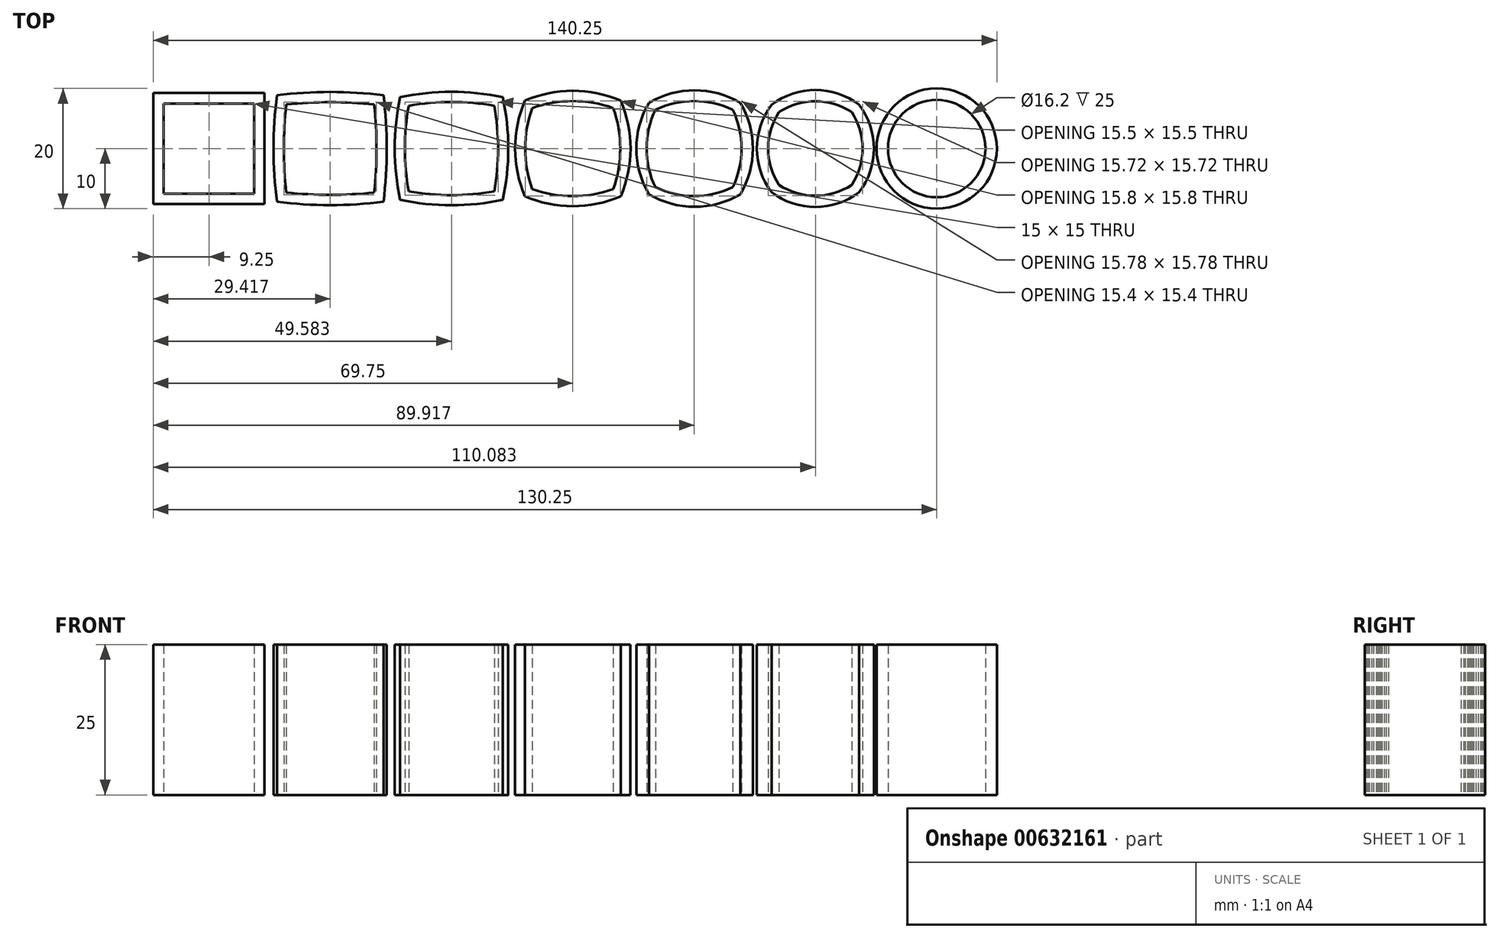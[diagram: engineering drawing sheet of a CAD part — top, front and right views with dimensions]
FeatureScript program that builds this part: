
annotation { "Feature Type Name" : "Feature", "Feature Type Description" : "" }
export const myFeature = defineFeature(function(context is Context, id is Id, definition is map)
    precondition{}
    {
        {
            var Q0;
            Q0=qCreatedBy(makeId("Top.planeOp"),FACE);
            var sketch = newSketch(context, id + "F0", { "sketchPlane" : qUnion([Q0])});
            skLineSegment(sketch, "E0", {"start": v(-60.5, 0) * mm, "end": v(-40.33, 0) * mm, "construction": true});
            skLineSegment(sketch, "E1", {"start": v(-40.33, 0) * mm, "end": v(-20.17, 0) * mm, "construction": true});
            skLineSegment(sketch, "E2", {"start": v(-20.17, 0) * mm, "end": v(0, 0) * mm, "construction": true});
            skLineSegment(sketch, "E3", {"start": v(0, 0) * mm, "end": v(20.17, 0) * mm, "construction": true});
            skLineSegment(sketch, "E4", {"start": v(20.17, 0) * mm, "end": v(40.33, 0) * mm, "construction": true});
            skLineSegment(sketch, "E5", {"start": v(40.33, 0) * mm, "end": v(60.5, 0) * mm, "construction": true});
            skCircle(sketch, "E6", {"center": v(60.5, 0) * mm, "radius": 8.1 * mm});
            skCircle(sketch, "E7", {"center": v(60.5, 0) * mm, "radius": 10 * mm});
            skLineSegment(sketch, "E8.bottom", {"start": v(-68, 7.5) * mm, "end": v(-53, 7.5) * mm});
            skLineSegment(sketch, "E8.top", {"start": v(-68, -7.5) * mm, "end": v(-53, -7.5) * mm});
            skLineSegment(sketch, "E8.left", {"start": v(-68, 7.5) * mm, "end": v(-68, -7.5) * mm});
            skLineSegment(sketch, "E8.right", {"start": v(-53, 7.5) * mm, "end": v(-53, -7.5) * mm});
            skPoint(sketch, "E8.middle", {"position": v(-60.5, 0) * mm});
            skLineSegment(sketch, "E9.bottom", {"start": v(-69.75, 9.25) * mm, "end": v(-51.25, 9.25) * mm});
            skLineSegment(sketch, "E9.top", {"start": v(-69.75, -9.25) * mm, "end": v(-51.25, -9.25) * mm});
            skLineSegment(sketch, "E9.left", {"start": v(-69.75, 9.25) * mm, "end": v(-69.75, -9.25) * mm});
            skLineSegment(sketch, "E9.right", {"start": v(-51.25, 9.25) * mm, "end": v(-51.25, -9.25) * mm});
            skArc(sketch, "E10", {"start": v(-33.02, -7.32) * mm, "mid": v(-32.63, 0) * mm, "end": v(-33.02, 7.32) * mm});
            skArc(sketch, "E11", {"start": v(-33.02, 7.32) * mm, "mid": v(-40.33, 7.7) * mm, "end": v(-47.65, 7.32) * mm});
            skArc(sketch, "E12", {"start": v(-47.65, 7.32) * mm, "mid": v(-48.03, 0) * mm, "end": v(-47.65, -7.32) * mm});
            skArc(sketch, "E13", {"start": v(-47.65, -7.32) * mm, "mid": v(-40.33, -7.7) * mm, "end": v(-33.02, -7.32) * mm});
            skArc(sketch, "E14", {"start": v(-31.48, -8.85) * mm, "mid": v(-30.92, 0) * mm, "end": v(-31.48, 8.85) * mm});
            skArc(sketch, "E15", {"start": v(-31.48, 8.85) * mm, "mid": v(-40.33, 9.41) * mm, "end": v(-49.18, 8.85) * mm});
            skArc(sketch, "E16", {"start": v(-49.18, 8.85) * mm, "mid": v(-49.75, 0) * mm, "end": v(-49.18, -8.85) * mm});
            skArc(sketch, "E17", {"start": v(-49.18, -8.85) * mm, "mid": v(-40.33, -9.41) * mm, "end": v(-31.48, -8.85) * mm});
            skArc(sketch, "E18", {"start": v(-13.05, -7.11) * mm, "mid": v(-12.42, 0) * mm, "end": v(-13.05, 7.11) * mm});
            skArc(sketch, "E19", {"start": v(-13.05, 7.11) * mm, "mid": v(-20.17, 7.75) * mm, "end": v(-27.28, 7.11) * mm});
            skArc(sketch, "E20", {"start": v(-27.28, 7.11) * mm, "mid": v(-27.92, 0) * mm, "end": v(-27.28, -7.11) * mm});
            skArc(sketch, "E21", {"start": v(-27.28, -7.11) * mm, "mid": v(-20.17, -7.75) * mm, "end": v(-13.05, -7.11) * mm});
            skArc(sketch, "E22", {"start": v(-11.64, -8.53) * mm, "mid": v(-10.72, 0) * mm, "end": v(-11.64, 8.53) * mm});
            skArc(sketch, "E23", {"start": v(-11.64, 8.53) * mm, "mid": v(-20.17, 9.45) * mm, "end": v(-28.7, 8.53) * mm});
            skArc(sketch, "E24", {"start": v(-28.7, 8.53) * mm, "mid": v(-29.61, 0) * mm, "end": v(-28.7, -8.53) * mm});
            skArc(sketch, "E25", {"start": v(-28.7, -8.53) * mm, "mid": v(-20.17, -9.45) * mm, "end": v(-11.64, -8.53) * mm});
            skArc(sketch, "E26", {"start": v(6.73, -6.73) * mm, "mid": v(7.9, 0) * mm, "end": v(6.73, 6.73) * mm});
            skArc(sketch, "E27", {"start": v(6.73, 6.73) * mm, "mid": v(0, 7.9) * mm, "end": v(-6.73, 6.73) * mm});
            skArc(sketch, "E28", {"start": v(-6.73, 6.73) * mm, "mid": v(-7.9, 0) * mm, "end": v(-6.73, -6.73) * mm});
            skArc(sketch, "E29", {"start": v(-6.73, -6.73) * mm, "mid": v(0, -7.9) * mm, "end": v(6.73, -6.73) * mm});
            skArc(sketch, "E30", {"start": v(7.95, -7.95) * mm, "mid": v(9.6, 0) * mm, "end": v(7.95, 7.95) * mm});
            skArc(sketch, "E31", {"start": v(7.95, 7.95) * mm, "mid": v(0, 9.6) * mm, "end": v(-7.95, 7.95) * mm});
            skArc(sketch, "E32", {"start": v(-7.95, 7.95) * mm, "mid": v(-9.6, 0) * mm, "end": v(-7.95, -7.95) * mm});
            skArc(sketch, "E33", {"start": v(-7.95, -7.95) * mm, "mid": v(0, -9.6) * mm, "end": v(7.95, -7.95) * mm});
            skArc(sketch, "E34", {"start": v(26.6, -6.44) * mm, "mid": v(28.06, 0) * mm, "end": v(26.6, 6.44) * mm});
            skArc(sketch, "E35", {"start": v(26.6, 6.44) * mm, "mid": v(20.17, 7.9) * mm, "end": v(13.73, 6.44) * mm});
            skArc(sketch, "E36", {"start": v(13.73, 6.44) * mm, "mid": v(12.28, 0) * mm, "end": v(13.73, -6.44) * mm});
            skArc(sketch, "E37", {"start": v(13.73, -6.44) * mm, "mid": v(20.17, -7.89) * mm, "end": v(26.6, -6.44) * mm});
            skArc(sketch, "E38", {"start": v(27.86, -7.6) * mm, "mid": v(29.93, 0) * mm, "end": v(27.86, 7.6) * mm});
            skArc(sketch, "E39", {"start": v(27.86, 7.6) * mm, "mid": v(20.25, 9.68) * mm, "end": v(12.65, 7.6) * mm});
            skArc(sketch, "E40", {"start": v(12.65, 7.6) * mm, "mid": v(10.57, 0) * mm, "end": v(12.65, -7.6) * mm});
            skArc(sketch, "E41", {"start": v(12.65, -7.6) * mm, "mid": v(20.25, -9.68) * mm, "end": v(27.86, -7.6) * mm});
            skArc(sketch, "E42", {"start": v(46.38, -6.05) * mm, "mid": v(48.2, 0) * mm, "end": v(46.38, 6.05) * mm});
            skArc(sketch, "E43", {"start": v(46.38, 6.05) * mm, "mid": v(40.33, 7.86) * mm, "end": v(34.29, 6.05) * mm});
            skArc(sketch, "E44", {"start": v(34.29, 6.05) * mm, "mid": v(32.47, 0) * mm, "end": v(34.29, -6.05) * mm});
            skArc(sketch, "E45", {"start": v(34.29, -6.05) * mm, "mid": v(40.33, -7.86) * mm, "end": v(46.38, -6.05) * mm});
            skArc(sketch, "E46", {"start": v(47.6, -7.27) * mm, "mid": v(50.06, 0) * mm, "end": v(47.6, 7.27) * mm});
            skArc(sketch, "E47", {"start": v(47.6, 7.27) * mm, "mid": v(40.33, 9.73) * mm, "end": v(33.06, 7.27) * mm});
            skArc(sketch, "E48", {"start": v(33.06, 7.27) * mm, "mid": v(30.6, 0) * mm, "end": v(33.06, -7.27) * mm});
            skArc(sketch, "E49", {"start": v(33.06, -7.27) * mm, "mid": v(40.33, -9.73) * mm, "end": v(47.6, -7.27) * mm});
            skSolve(sketch);
        }
        {
            var Q0;
            Q0=makeQuery(id+"F0.imprint","IMPRINT",FACE,{"disambiguationData":[TD([[makeQuery(id+"F0.imprint","IMPRINT",EDGE,{"derivedFrom":sQuery(id+"F0.wireOp",EDGE,"E18")}),-1.0]])]});
            var Q1;
            Q1=makeQuery(id+"F0.imprint","IMPRINT",FACE,{"disambiguationData":[TD([[makeQuery(id+"F0.imprint","IMPRINT",EDGE,{"derivedFrom":sQuery(id+"F0.wireOp",EDGE,"E10")}),-1.0]])]});
            var Q2;
            Q2=makeQuery(id+"F0.imprint","IMPRINT",FACE,{"disambiguationData":[TD([[makeQuery(id+"F0.imprint","IMPRINT",EDGE,{"derivedFrom":sQuery(id+"F0.wireOp",EDGE,"E8.bottom")}),1.0]])]});
            var Q3;
            Q3=makeQuery(id+"F0.imprint","IMPRINT",FACE,{"disambiguationData":[TD([[makeQuery(id+"F0.imprint","IMPRINT",EDGE,{"derivedFrom":sQuery(id+"F0.wireOp",EDGE,"E26")}),-1.0]])]});
            var Q4;
            Q4=makeQuery(id+"F0.imprint","IMPRINT",FACE,{"disambiguationData":[TD([[makeQuery(id+"F0.imprint","IMPRINT",EDGE,{"derivedFrom":sQuery(id+"F0.wireOp",EDGE,"E34")}),-1.0]])]});
            var Q5;
            Q5=makeQuery(id+"F0.imprint","IMPRINT",FACE,{"disambiguationData":[TD([[makeQuery(id+"F0.imprint","IMPRINT",EDGE,{"derivedFrom":sQuery(id+"F0.wireOp",EDGE,"E42")}),-1.0]])]});
            var Q6;
            Q6=makeQuery(id+"F0.imprint","IMPRINT",FACE,{"disambiguationData":[TD([[makeQuery(id+"F0.imprint","IMPRINT",EDGE,{"derivedFrom":sQuery(id+"F0.wireOp",EDGE,"E6")}),-1.0]])]});
            extrude(context, id + "F1", {"entities" : qUnion([Q0, Q1, Q2, Q3, Q4, Q5, Q6]), "depth" : 25 * mm, "offsetDistance" : 25 * mm});
        }
    });
